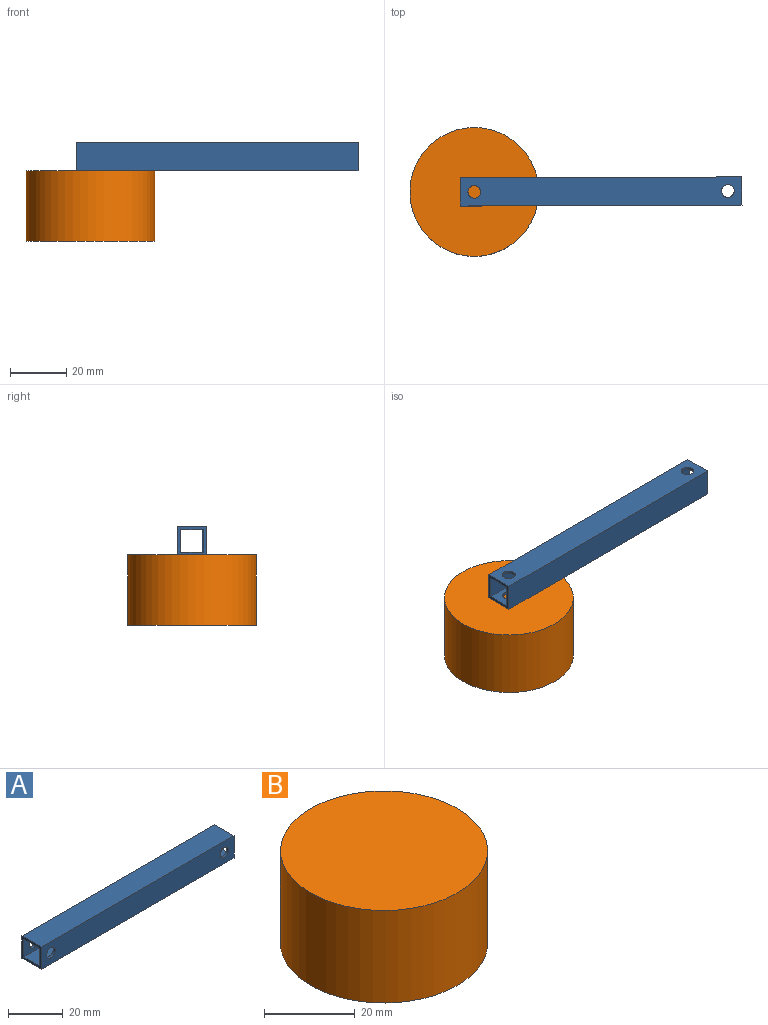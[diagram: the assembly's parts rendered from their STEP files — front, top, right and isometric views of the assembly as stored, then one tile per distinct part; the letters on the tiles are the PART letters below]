
ASSEMBLY  parts=2 mates=1
PART A: 14 faces, bbox 100x10x10 mm
  f0: plane 10x10mm, normal (1,0,0), area 36mm2, adj f2,f3,f4,f5,f6,f7,f8,f9
  f1: plane 10x10mm, normal (-1,0,0), area 36mm2, adj f2,f3,f4,f5,f6,f7,f8,f9
  f2: plane 100x10mm, normal (0,1,0), area 968.2mm2, adj f0,f1,f3,f5,f12,f13
  f3: plane 100x10mm, normal (0,0,1), area 1000mm2, adj f0,f1,f2,f4
  f4: plane 100x10mm, normal (0,-1,0), area 968.2mm2, adj f0,f1,f3,f5,f10,f11
  f5: plane 100x10mm, normal (0,0,-1), area 1000mm2, adj f0,f1,f2,f4
  f6: plane 100x8mm, normal (0,-1,0), area 768.2mm2, adj f0,f1,f7,f9,f12,f13
  f7: plane 100x8mm, normal (0,0,-1), area 800mm2, adj f0,f1,f6,f8
  f8: plane 100x8mm, normal (0,1,0), area 768.2mm2, adj f0,f1,f7,f9,f10,f11
  f9: plane 100x8mm, normal (0,0,1), area 800mm2, adj f0,f1,f6,f8
  f10: cylinder r=2.25mm len=4.5mm, axis (0,-1,0), area 14.1mm2, adj f4,f8
  f11: cylinder r=2.25mm len=4.5mm, axis (0,-1,0), area 14.1mm2, adj f4,f8
  f12: cylinder r=2.25mm len=4.5mm, axis (0,-1,0), area 14.1mm2, adj f2,f6
  f13: cylinder r=2.25mm len=4.5mm, axis (0,-1,0), area 14.1mm2, adj f2,f6
PART B: 3 faces, bbox 45.7x45.7x25 mm
  f0: cylinder r=22.86mm len=45.72mm, axis (0,0,-1), area 3591mm2, adj f1,f2
  f1: plane 45.72x45.72mm, normal (0,0,1), area 1641.9mm2, adj f0
  f2: plane 45.72x45.72mm, normal (0,0,-1), area 1641.9mm2, adj f0
PLACE A rot(axis=(0,-0.71,-0.71),179.9deg) t=(45,0.15,30)mm
PLACE B t=(46.43,58.25,0)mm
MATE revolute A.f10 <-> B.f0  axis (0,0,-1) through (0,0,25)mm
